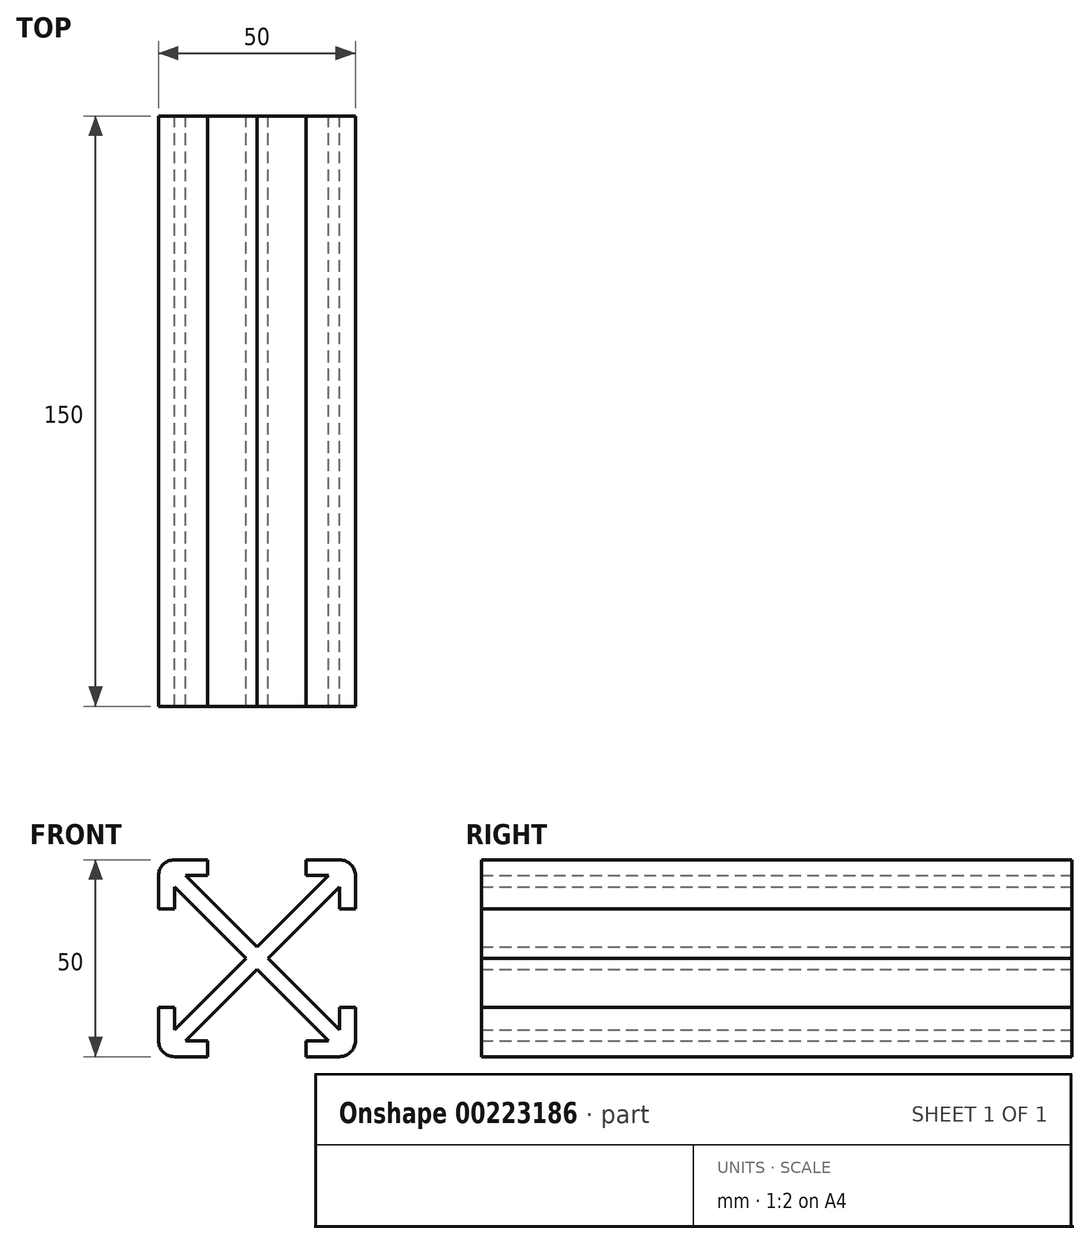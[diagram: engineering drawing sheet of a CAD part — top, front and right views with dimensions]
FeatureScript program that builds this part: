
annotation { "Feature Type Name" : "Feature", "Feature Type Description" : "" }
export const myFeature = defineFeature(function(context is Context, id is Id, definition is map)
    precondition{}
    {
        {
            var Q0;
            Q0=qCreatedBy(makeId("Front.planeOp"),FACE);
            var sketch = newSketch(context, id + "F0", { "sketchPlane" : qUnion([Q0])});
            skLineSegment(sketch, "E0", {"start": v(0, 0) * mm, "end": v(27.95, 27.95) * mm, "construction": true});
            skLineSegment(sketch, "E1", {"start": v(0, 0) * mm, "end": v(40.18, 0) * mm, "construction": true});
            skLineSegment(sketch, "E2", {"start": v(0, 25) * mm, "end": v(36.09, 25) * mm, "construction": true});
            skLineSegment(sketch, "E3", {"start": v(25, 0) * mm, "end": v(25, 25) * mm, "construction": true});
            skLineSegment(sketch, "E4", {"start": v(12.5, 0) * mm, "end": v(12.5, 25) * mm, "construction": true});
            skLineSegment(sketch, "E5", {"start": v(12.5, 25) * mm, "end": v(21, 25) * mm});
            skLineSegment(sketch, "E6", {"start": v(25, 21) * mm, "end": v(25, 12.5) * mm});
            skLineSegment(sketch, "E7", {"start": v(12.5, 25) * mm, "end": v(12.5, 21) * mm});
            skLineSegment(sketch, "E8", {"start": v(12.5, 21) * mm, "end": v(18.17, 21) * mm});
            skLineSegment(sketch, "E9", {"start": v(21, 18.17) * mm, "end": v(21, 12.5) * mm});
            skLineSegment(sketch, "E10", {"start": v(21, 12.5) * mm, "end": v(25, 12.5) * mm});
            skPoint(sketch, "E11.visualSharp", {"position": v(25, 25) * mm});
            skArc(sketch, "E11.filletArc", {"start": v(25, 21) * mm, "mid": v(23.83, 23.83) * mm, "end": v(21, 25) * mm});
            skLineSegment(sketch, "E12", {"start": v(0, 2.83) * mm, "end": v(18.17, 21) * mm});
            skLineSegment(sketch, "E13.MirrorCS", {"start": v(2.83, 0) * mm, "end": v(21, 18.17) * mm});
            skLineSegment(sketch, "E14.1.0", {"start": v(-2.83, 0) * mm, "end": v(-21, 18.17) * mm});
            skLineSegment(sketch, "E14.1.1", {"start": v(-21, 12.5) * mm, "end": v(-21, 18.17) * mm});
            skLineSegment(sketch, "E14.1.2", {"start": v(-25, 12.5) * mm, "end": v(-21, 12.5) * mm});
            skLineSegment(sketch, "E14.1.3", {"start": v(-25, 12.5) * mm, "end": v(-25, 21) * mm});
            skArc(sketch, "E14.1.4", {"start": v(-21, 25) * mm, "mid": v(-23.83, 23.83) * mm, "end": v(-25, 21) * mm});
            skLineSegment(sketch, "E14.1.5", {"start": v(-21, 25) * mm, "end": v(-12.5, 25) * mm});
            skLineSegment(sketch, "E14.1.6", {"start": v(-12.5, 21) * mm, "end": v(-12.5, 25) * mm});
            skLineSegment(sketch, "E14.1.7", {"start": v(-18.17, 21) * mm, "end": v(-12.5, 21) * mm});
            skLineSegment(sketch, "E14.1.8", {"start": v(0, 2.83) * mm, "end": v(-18.17, 21) * mm});
            skLineSegment(sketch, "E14.1.9", {"start": v(0, 0) * mm, "end": v(0, 40.18) * mm, "construction": true});
            skLineSegment(sketch, "E14.2.0", {"start": v(0, -2.83) * mm, "end": v(-18.17, -21) * mm});
            skLineSegment(sketch, "E14.2.1", {"start": v(-12.5, -21) * mm, "end": v(-18.17, -21) * mm});
            skLineSegment(sketch, "E14.2.2", {"start": v(-12.5, -25) * mm, "end": v(-12.5, -21) * mm});
            skLineSegment(sketch, "E14.2.3", {"start": v(-12.5, -25) * mm, "end": v(-21, -25) * mm});
            skArc(sketch, "E14.2.4", {"start": v(-25, -21) * mm, "mid": v(-23.83, -23.83) * mm, "end": v(-21, -25) * mm});
            skLineSegment(sketch, "E14.2.5", {"start": v(-25, -21) * mm, "end": v(-25, -12.5) * mm});
            skLineSegment(sketch, "E14.2.6", {"start": v(-21, -12.5) * mm, "end": v(-25, -12.5) * mm});
            skLineSegment(sketch, "E14.2.7", {"start": v(-21, -18.17) * mm, "end": v(-21, -12.5) * mm});
            skLineSegment(sketch, "E14.2.8", {"start": v(-2.83, 0) * mm, "end": v(-21, -18.17) * mm});
            skLineSegment(sketch, "E14.2.9", {"start": v(0, 0) * mm, "end": v(-40.18, 0) * mm, "construction": true});
            skLineSegment(sketch, "E14.3.0", {"start": v(2.83, 0) * mm, "end": v(21, -18.17) * mm});
            skLineSegment(sketch, "E14.3.1", {"start": v(21, -12.5) * mm, "end": v(21, -18.17) * mm});
            skLineSegment(sketch, "E14.3.2", {"start": v(25, -12.5) * mm, "end": v(21, -12.5) * mm});
            skLineSegment(sketch, "E14.3.3", {"start": v(25, -12.5) * mm, "end": v(25, -21) * mm});
            skArc(sketch, "E14.3.4", {"start": v(21, -25) * mm, "mid": v(23.83, -23.83) * mm, "end": v(25, -21) * mm});
            skLineSegment(sketch, "E14.3.5", {"start": v(21, -25) * mm, "end": v(12.5, -25) * mm});
            skLineSegment(sketch, "E14.3.6", {"start": v(12.5, -21) * mm, "end": v(12.5, -25) * mm});
            skLineSegment(sketch, "E14.3.7", {"start": v(18.17, -21) * mm, "end": v(12.5, -21) * mm});
            skLineSegment(sketch, "E14.3.8", {"start": v(0, -2.83) * mm, "end": v(18.17, -21) * mm});
            skLineSegment(sketch, "E14.3.9", {"start": v(0, 0) * mm, "end": v(0, -40.18) * mm, "construction": true});
            skPoint(sketch, "E14.center", {"position": v(0, 0) * mm});
            skSolve(sketch);
        }
        {
            var Q0;
            Q0 = qSketchRegion(id + "F0", true);
            extrude(context, id + "F1", {"entities" : qUnion([Q0]), "endBound" : BoundingType.SYMMETRIC, "depth" : 150 * mm});
        }
    });
